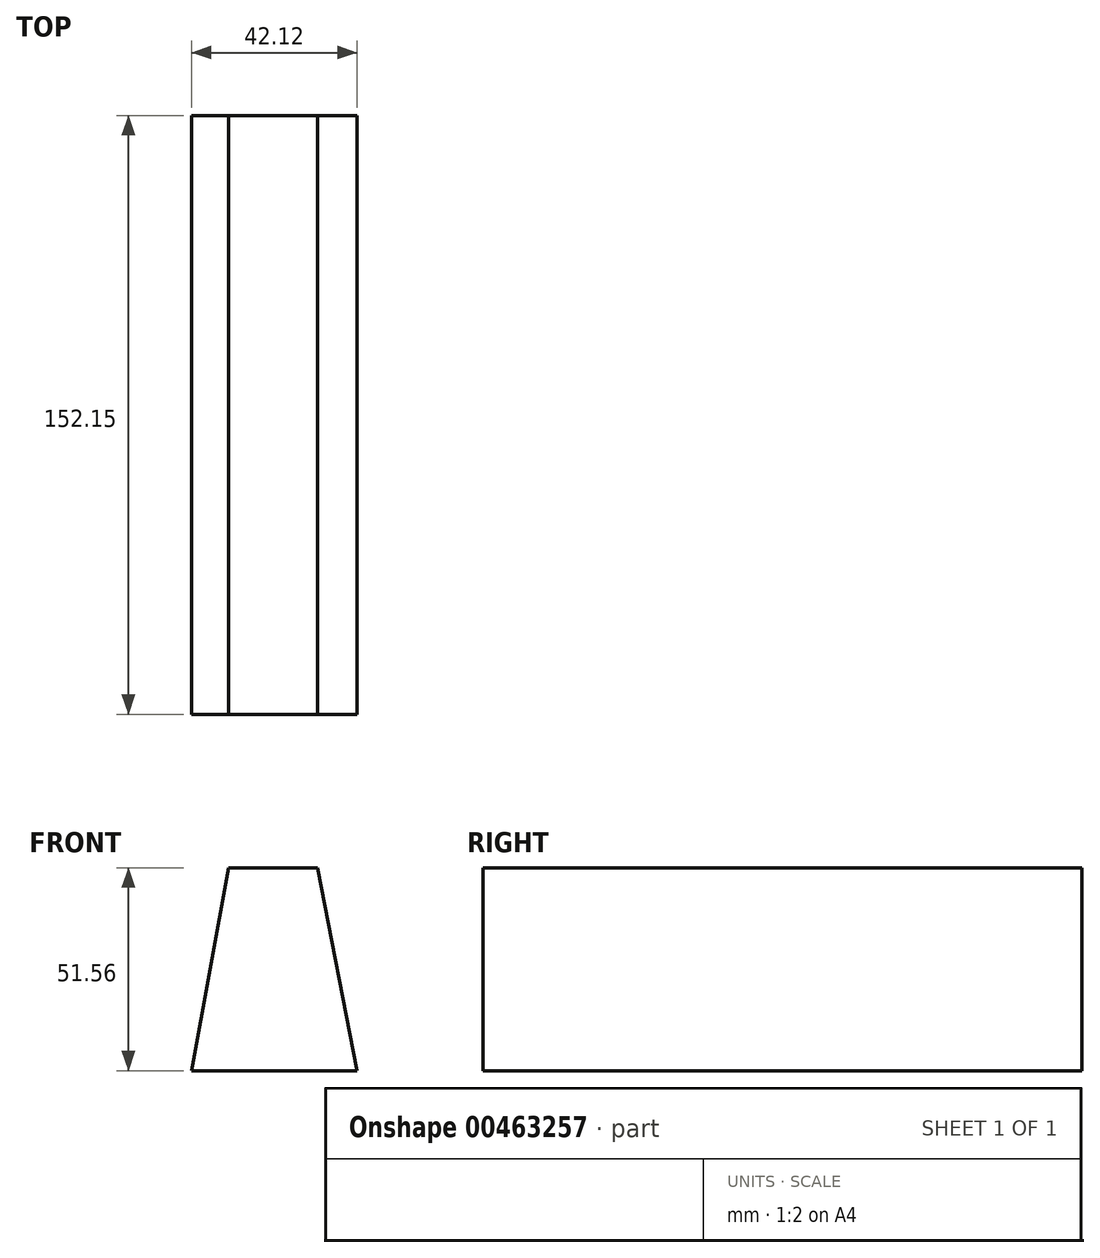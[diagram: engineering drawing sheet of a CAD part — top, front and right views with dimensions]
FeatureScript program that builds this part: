
annotation { "Feature Type Name" : "Feature", "Feature Type Description" : "" }
export const myFeature = defineFeature(function(context is Context, id is Id, definition is map)
    precondition{}
    {
        {
            var Q0;
            Q0=qCreatedBy(makeId("Front.planeOp"),FACE);
            var sketch = newSketch(context, id + "F0", { "sketchPlane" : qUnion([Q0])});
            skLineSegment(sketch, "E0", {"start": v(-18.86, -15.56) * mm, "end": v(23.26, -15.56) * mm});
            skLineSegment(sketch, "E1", {"start": v(23.26, -15.56) * mm, "end": v(13.2, 36) * mm});
            skLineSegment(sketch, "E2", {"start": v(-9.43, 36) * mm, "end": v(-18.86, -15.56) * mm});
            skLineSegment(sketch, "E3", {"start": v(-9.43, 36) * mm, "end": v(13.2, 36) * mm});
            skSolve(sketch);
        }
        {
            var Q0;
            Q0=makeQuery(id+"F0.imprint","IMPRINT",FACE,{"disambiguationData":[TD([[makeQuery(id+"F0.imprint","IMPRINT",EDGE,{"derivedFrom":sQuery(id+"F0.wireOp",EDGE,"E0")}),1.0]])]});
            extrude(context, id + "F1", {"entities" : qUnion([Q0]), "depth" : 152.15 * mm});
        }
    });
